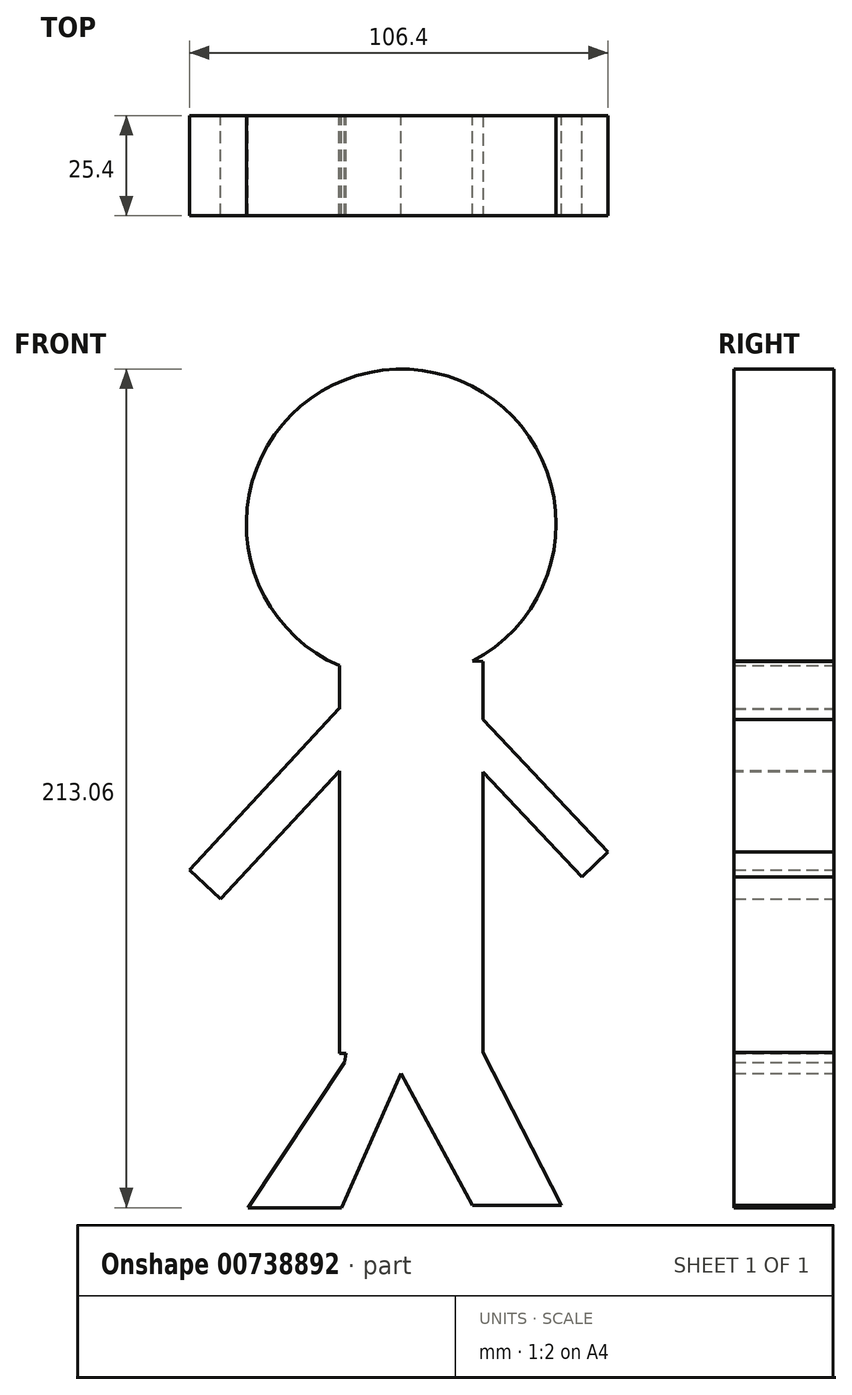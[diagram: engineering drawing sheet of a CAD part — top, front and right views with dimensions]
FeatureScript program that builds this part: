
annotation { "Feature Type Name" : "Feature", "Feature Type Description" : "" }
export const myFeature = defineFeature(function(context is Context, id is Id, definition is map)
    precondition{}
    {
        {
            var Q0;
            Q0=qCreatedBy(makeId("Front.planeOp"),FACE);
            var sketch = newSketch(context, id + "F0", { "sketchPlane" : qUnion([Q0])});
            skCircle(sketch, "E0", {"center": v(0, 58.04) * mm, "radius": 39.33 * mm});
            skLineSegment(sketch, "E1", {"start": v(-16.15, 15) * mm, "end": v(-16.15, 15) * mm});
            skSolve(sketch);
        }
        {
            var Q0;
            Q0=makeQuery(id+"F0.imprint","IMPRINT",FACE,{"disambiguationData":[TD([[makeQuery(id+"F0.imprint","IMPRINT",EDGE,{"derivedFrom":sQuery(id+"F0.wireOp",EDGE,"E0")}),1.0]])]});
            extrude(context, id + "F1", {"entities" : qUnion([Q0]), "depth" : 25.4 * mm, "offsetDistance" : 25.4 * mm});
        }
        {
            var Q0;
            Q0=qCreatedBy(makeId("Front.planeOp"),FACE);
            var sketch = newSketch(context, id + "F2", { "sketchPlane" : qUnion([Q0])});
            skLineSegment(sketch, "E2", {"start": v(-15.71, 23.5) * mm, "end": v(-15.71, -76.47) * mm});
            skLineSegment(sketch, "E3", {"start": v(-15.71, -76.47) * mm, "end": v(20.8, -76.47) * mm});
            skLineSegment(sketch, "E4", {"start": v(20.8, -76.47) * mm, "end": v(20.8, 23.11) * mm});
            skLineSegment(sketch, "E5", {"start": v(20.8, 23.11) * mm, "end": v(-15.71, 23.5) * mm});
            skSolve(sketch);
        }
        {
            var Q0;
            Q0 = qSketchRegion(id + "F2", true);
            extrude(context, id + "F3", {"entities" : qUnion([Q0]), "operationType" : NewBodyOperationType.ADD, "depth" : 25.4 * mm, "offsetDistance" : 25.4 * mm});
        }
        {
            var Q0;
            Q0=qCreatedBy(makeId("Front.planeOp"),FACE);
            var sketch = newSketch(context, id + "F4", { "sketchPlane" : qUnion([Q0])});
            skLineSegment(sketch, "E6", {"start": v(-15.76, 11.09) * mm, "end": v(-53.82, -29.89) * mm});
            skLineSegment(sketch, "E7", {"start": v(-53.82, -29.89) * mm, "end": v(-45.93, -37.22) * mm});
            skLineSegment(sketch, "E8", {"start": v(-45.93, -37.22) * mm, "end": v(-11.35, 0) * mm});
            skLineSegment(sketch, "E9", {"start": v(-11.35, 0) * mm, "end": v(-15.76, 11.09) * mm});
            skLineSegment(sketch, "E10", {"start": v(20.55, 8.64) * mm, "end": v(52.58, -25.37) * mm});
            skLineSegment(sketch, "E11", {"start": v(52.58, -25.37) * mm, "end": v(45.9, -31.68) * mm});
            skLineSegment(sketch, "E12", {"start": v(45.9, -31.68) * mm, "end": v(16.06, 0) * mm});
            skLineSegment(sketch, "E13", {"start": v(16.06, 0) * mm, "end": v(20.55, 8.64) * mm});
            skLineSegment(sketch, "E14", {"start": v(-28.64, -18.6) * mm, "end": v(-28.64, -18.6) * mm});
            skSolve(sketch);
        }
        {
            var Q0;
            Q0 = qSketchRegion(id + "F4", true);
            extrude(context, id + "F5", {"entities" : qUnion([Q0]), "operationType" : NewBodyOperationType.ADD, "depth" : 25.4 * mm, "offsetDistance" : 25.4 * mm});
        }
        {
            var Q0;
            Q0=qCreatedBy(makeId("Front.planeOp"),FACE);
            var sketch = newSketch(context, id + "F6", { "sketchPlane" : qUnion([Q0])});
            skLineSegment(sketch, "E15", {"start": v(-14.4, -78.84) * mm, "end": v(-38.89, -115.7) * mm});
            skLineSegment(sketch, "E16", {"start": v(-38.89, -115.7) * mm, "end": v(-15.16, -115.7) * mm});
            skLineSegment(sketch, "E17", {"start": v(-15.16, -115.7) * mm, "end": v(0, -81.53) * mm});
            skLineSegment(sketch, "E18", {"start": v(0, -81.53) * mm, "end": v(0, -69.34) * mm});
            skLineSegment(sketch, "E19", {"start": v(0, -69.34) * mm, "end": v(-12.7, -69.34) * mm});
            skLineSegment(sketch, "E20", {"start": v(-12.7, -69.34) * mm, "end": v(-14.4, -78.84) * mm});
            skLineSegment(sketch, "E21", {"start": v(17.3, -69.34) * mm, "end": v(6.92, -69.34) * mm});
            skLineSegment(sketch, "E22", {"start": v(6.92, -69.34) * mm, "end": v(0, -69.34) * mm});
            skLineSegment(sketch, "E23", {"start": v(0, -81.53) * mm, "end": v(18.05, -115.13) * mm});
            skLineSegment(sketch, "E24", {"start": v(18.05, -115.13) * mm, "end": v(40.68, -115.13) * mm});
            skLineSegment(sketch, "E25", {"start": v(40.68, -115.13) * mm, "end": v(17.3, -69.34) * mm});
            skSolve(sketch);
        }
        {
            var Q0;
            Q0 = qSketchRegion(id + "F6", true);
            extrude(context, id + "F7", {"entities" : qUnion([Q0]), "operationType" : NewBodyOperationType.ADD, "depth" : 25.4 * mm, "offsetDistance" : 25.4 * mm});
        }
    });
